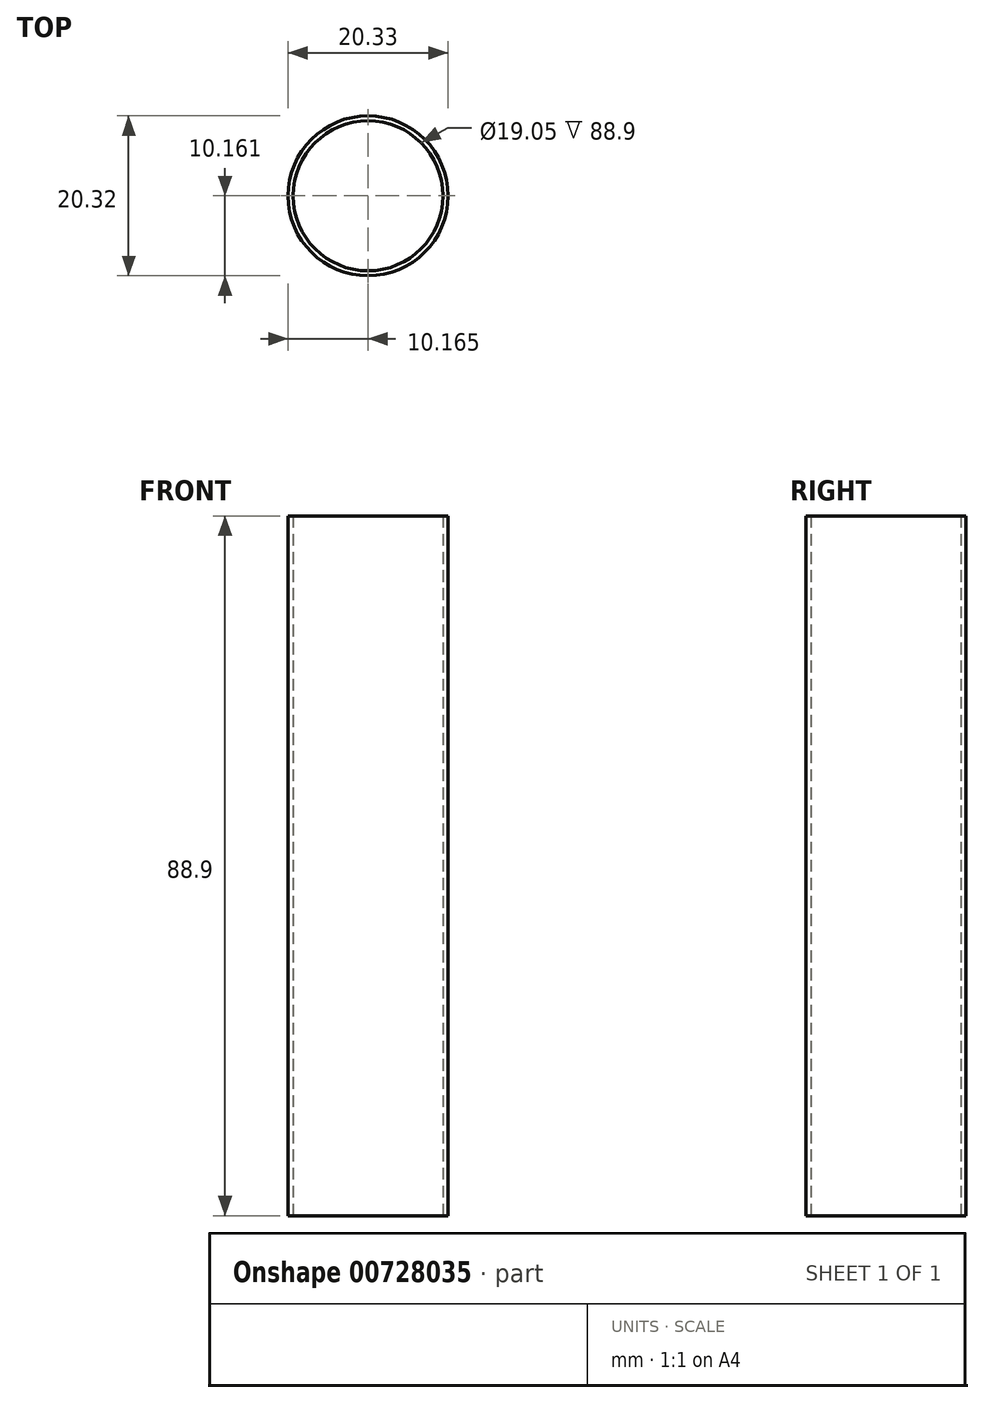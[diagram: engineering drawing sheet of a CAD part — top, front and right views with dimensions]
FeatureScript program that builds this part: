
annotation { "Feature Type Name" : "Feature", "Feature Type Description" : "" }
export const myFeature = defineFeature(function(context is Context, id is Id, definition is map)
    precondition{}
    {
        {
            var Q0;
            Q0=qCreatedBy(makeId("Top.planeOp"),FACE);
            var sketch = newSketch(context, id + "F0", { "sketchPlane" : qUnion([Q0])});
            skCircle(sketch, "E0", {"center": v(3.18, 1.2) * mm, "radius": 9.53 * mm});
            skPoint(sketch, "E0.centerSnap0", {"position": v(3.18, 4.37) * mm});
            skPoint(sketch, "E0.centerSnap1", {"position": v(-9.52, 1.2) * mm});
            skCircle(sketch, "E1", {"center": v(3.18, 1.2) * mm, "radius": 10.16 * mm});
            skSolve(sketch);
        }
        {
            var Q0;
            Q0 = qSketchRegion(id + "F0", true);
            extrude(context, id + "F1", {"entities" : qUnion([Q0]), "depth" : 88.9 * mm, "offsetDistance" : 25.4 * mm});
        }
    });
